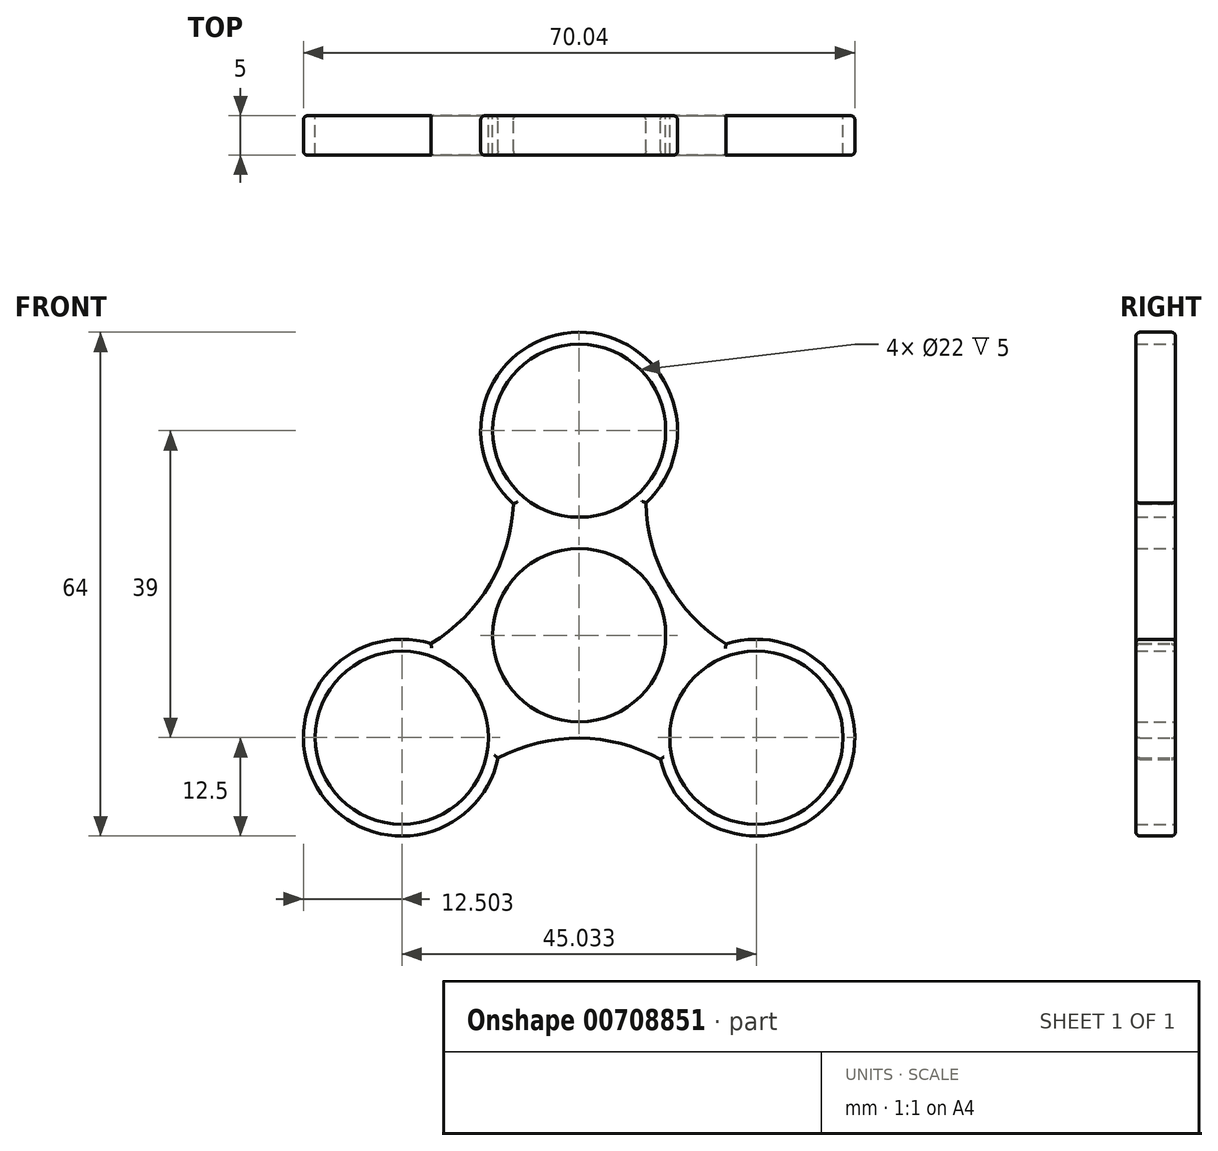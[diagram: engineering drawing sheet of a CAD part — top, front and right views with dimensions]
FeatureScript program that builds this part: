
annotation { "Feature Type Name" : "Feature", "Feature Type Description" : "" }
export const myFeature = defineFeature(function(context is Context, id is Id, definition is map)
    precondition{}
    {
        {
            var Q0;
            Q0=qCreatedBy(makeId("Front.planeOp"),FACE);
            var sketch = newSketch(context, id + "F0", { "sketchPlane" : qUnion([Q0])});
            skCircle(sketch, "E0", {"center": v(0, 0) * mm, "radius": 11 * mm});
            skCircle(sketch, "E1", {"center": v(22.52, -13) * mm, "radius": 11 * mm});
            skArc(sketch, "E2", {"start": v(10.33, -15.76) * mm, "mid": v(33.38, -19.18) * mm, "end": v(18.65, -1.11) * mm});
            skCircle(sketch, "E3", {"center": v(-22.52, -13) * mm, "radius": 11 * mm});
            skArc(sketch, "E4", {"start": v(-18.81, -1.06) * mm, "mid": v(-33.3, -19.32) * mm, "end": v(-10.29, -15.6) * mm});
            skCircle(sketch, "E5", {"center": v(0, 26) * mm, "radius": 11 * mm});
            skArc(sketch, "E6", {"start": v(8.49, 16.82) * mm, "mid": v(-0.09, 38.5) * mm, "end": v(-8.36, 16.7) * mm});
            skArc(sketch, "E7", {"start": v(10.33, -15.76) * mm, "mid": v(0.04, -13.07) * mm, "end": v(-10.29, -15.6) * mm});
            skArc(sketch, "E8.1.0", {"start": v(8.49, 16.82) * mm, "mid": v(11.3, 6.57) * mm, "end": v(18.65, -1.11) * mm});
            skArc(sketch, "E8.2.0", {"start": v(-18.81, -1.06) * mm, "mid": v(-11.34, 6.5) * mm, "end": v(-8.36, 16.7) * mm});
            skSolve(sketch);
        }
        {
            var Q0;
            Q0 = qSketchRegion(id + "F0", true);
            extrude(context, id + "F1", {"entities" : qUnion([Q0]), "depth" : 5 * mm, "offsetDistance" : 25 * mm});
        }
        {
            var Q0;
            Q0=makeQuery(id+"F1.opExtrude","CAP_EDGE",EDGE,{"disambiguationData":[OSD([sQuery(id+"F0.wireOp",EDGE,"E7")])],"isStart":false});
            var Q1;
            Q1=makeQuery(id+"F1.opExtrude","CAP_EDGE",EDGE,{"disambiguationData":[OSD([sQuery(id+"F0.wireOp",EDGE,"E8.2.0")])],"isStart":false});
            var Q2;
            Q2=makeQuery(id+"F1.opExtrude","CAP_EDGE",EDGE,{"disambiguationData":[OSD([sQuery(id+"F0.wireOp",EDGE,"E6")])],"isStart":false});
            var Q3;
            Q3=makeQuery(id+"F1.opExtrude","CAP_EDGE",EDGE,{"disambiguationData":[OSD([sQuery(id+"F0.wireOp",EDGE,"E8.1.0")])],"isStart":false});
            var Q4;
            Q4=makeQuery(id+"F1.opExtrude","CAP_EDGE",EDGE,{"disambiguationData":[OSD([sQuery(id+"F0.wireOp",EDGE,"E2")])],"isStart":false});
            var Q5;
            Q5=makeQuery(id+"F1.opExtrude","CAP_EDGE",EDGE,{"disambiguationData":[OSD([sQuery(id+"F0.wireOp",EDGE,"E2")])],"isStart":true});
            var Q6;
            Q6=makeQuery(id+"F1.opExtrude","CAP_EDGE",EDGE,{"disambiguationData":[OSD([sQuery(id+"F0.wireOp",EDGE,"E4")])],"isStart":false});
            var Q7;
            Q7=makeQuery(id+"F1.opExtrude","CAP_EDGE",EDGE,{"disambiguationData":[OSD([sQuery(id+"F0.wireOp",EDGE,"E7")])],"isStart":true});
            var Q8;
            Q8=makeQuery(id+"F1.opExtrude","CAP_EDGE",EDGE,{"disambiguationData":[OSD([sQuery(id+"F0.wireOp",EDGE,"E4")])],"isStart":true});
            var Q9;
            Q9=makeQuery(id+"F1.opExtrude","CAP_EDGE",EDGE,{"disambiguationData":[OSD([sQuery(id+"F0.wireOp",EDGE,"E8.2.0")])],"isStart":true});
            var Q10;
            Q10=makeQuery(id+"F1.opExtrude","CAP_EDGE",EDGE,{"disambiguationData":[OSD([sQuery(id+"F0.wireOp",EDGE,"E8.1.0")])],"isStart":true});
            var Q11;
            Q11=makeQuery(id+"F1.opExtrude","CAP_EDGE",EDGE,{"disambiguationData":[OSD([sQuery(id+"F0.wireOp",EDGE,"E6")])],"isStart":true});
            fillet(context, id + "F2", {"entities" : qUnion([Q0, Q1, Q2, Q3, Q4, Q5, Q6, Q7, Q8, Q9, Q10, Q11]), "radius" : .5 * mm, "tangentPropagation" : true, "allowEdgeOverflow" : false});
        }
    });
